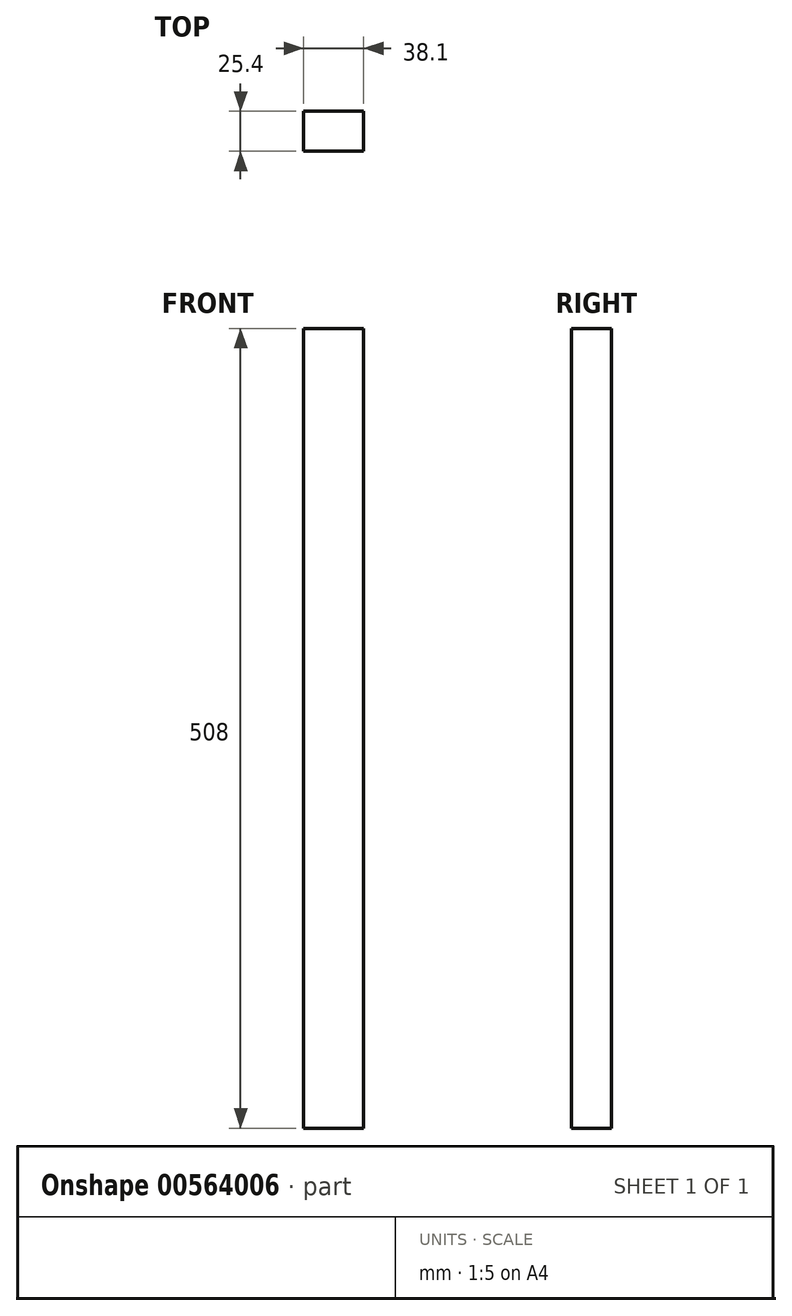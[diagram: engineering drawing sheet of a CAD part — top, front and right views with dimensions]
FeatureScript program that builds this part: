
annotation { "Feature Type Name" : "Feature", "Feature Type Description" : "" }
export const myFeature = defineFeature(function(context is Context, id is Id, definition is map)
    precondition{}
    {
        {
            var Q0;
            Q0=qCreatedBy(makeId("Front.planeOp"),FACE);
            var sketch = newSketch(context, id + "F0", { "sketchPlane" : qUnion([Q0])});
            skLineSegment(sketch, "E0.bottom", {"start": v(19.05, -254) * mm, "end": v(-19.05, -254) * mm});
            skLineSegment(sketch, "E0.top", {"start": v(19.05, 254) * mm, "end": v(-19.05, 254) * mm});
            skLineSegment(sketch, "E0.left", {"start": v(19.05, -254) * mm, "end": v(19.05, 254) * mm});
            skLineSegment(sketch, "E0.right", {"start": v(-19.05, -254) * mm, "end": v(-19.05, 254) * mm});
            skPoint(sketch, "E0.middle", {"position": v(0, 0) * mm});
            skSolve(sketch);
        }
        {
            var Q0;
            Q0=makeQuery(id+"F0.imprint","IMPRINT",FACE,{"disambiguationData":[TD([[makeQuery(id+"F0.imprint","IMPRINT",EDGE,{"derivedFrom":sQuery(id+"F0.wireOp",EDGE,"E0.bottom")}),-1.0]])]});
            extrude(context, id + "F1", {"entities" : qUnion([Q0]), "depth" : 25.4 * mm, "offsetDistance" : 25.4 * mm});
        }
    });
